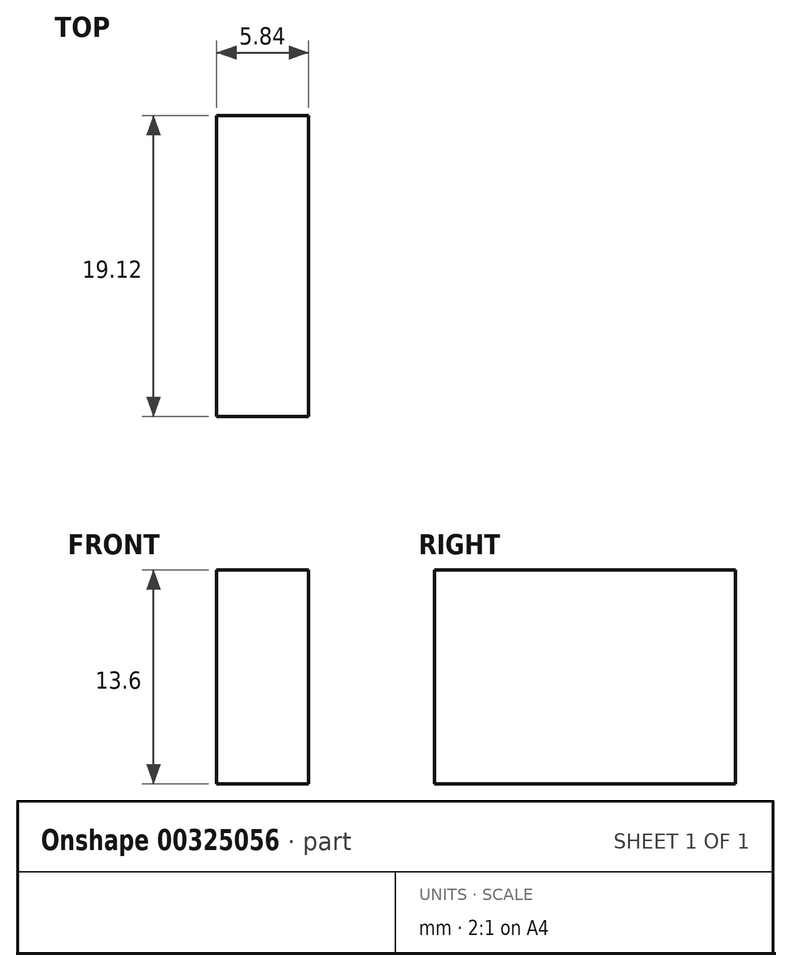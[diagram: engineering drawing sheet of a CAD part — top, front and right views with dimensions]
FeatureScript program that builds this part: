
annotation { "Feature Type Name" : "Feature", "Feature Type Description" : "" }
export const myFeature = defineFeature(function(context is Context, id is Id, definition is map)
    precondition{}
    {
        {
            var Q0;
            Q0=qCreatedBy(makeId("Top.planeOp"),FACE);
            var sketch = newSketch(context, id + "F0", { "sketchPlane" : qUnion([Q0])});
            skLineSegment(sketch, "E0.bottom", {"start": v(-18.17, 6.15) * mm, "end": v(-12.33, 6.15) * mm});
            skLineSegment(sketch, "E0.top", {"start": v(-18.17, -12.97) * mm, "end": v(-12.33, -12.97) * mm});
            skLineSegment(sketch, "E0.left", {"start": v(-18.17, 6.15) * mm, "end": v(-18.17, -12.97) * mm});
            skLineSegment(sketch, "E0.right", {"start": v(-12.33, 6.15) * mm, "end": v(-12.33, -12.97) * mm});
            skSolve(sketch);
        }
        {
            var Q0;
            Q0=makeQuery(id+"F0.imprint","IMPRINT",FACE,{"disambiguationData":[TD([[makeQuery(id+"F0.imprint","IMPRINT",EDGE,{"derivedFrom":sQuery(id+"F0.wireOp",EDGE,"E0.bottom")}),-1.0]])]});
            extrude(context, id + "F1", {"entities" : qUnion([Q0]), "oppositeDirection" : true, "depth" : 13.6 * mm});
        }
    });
